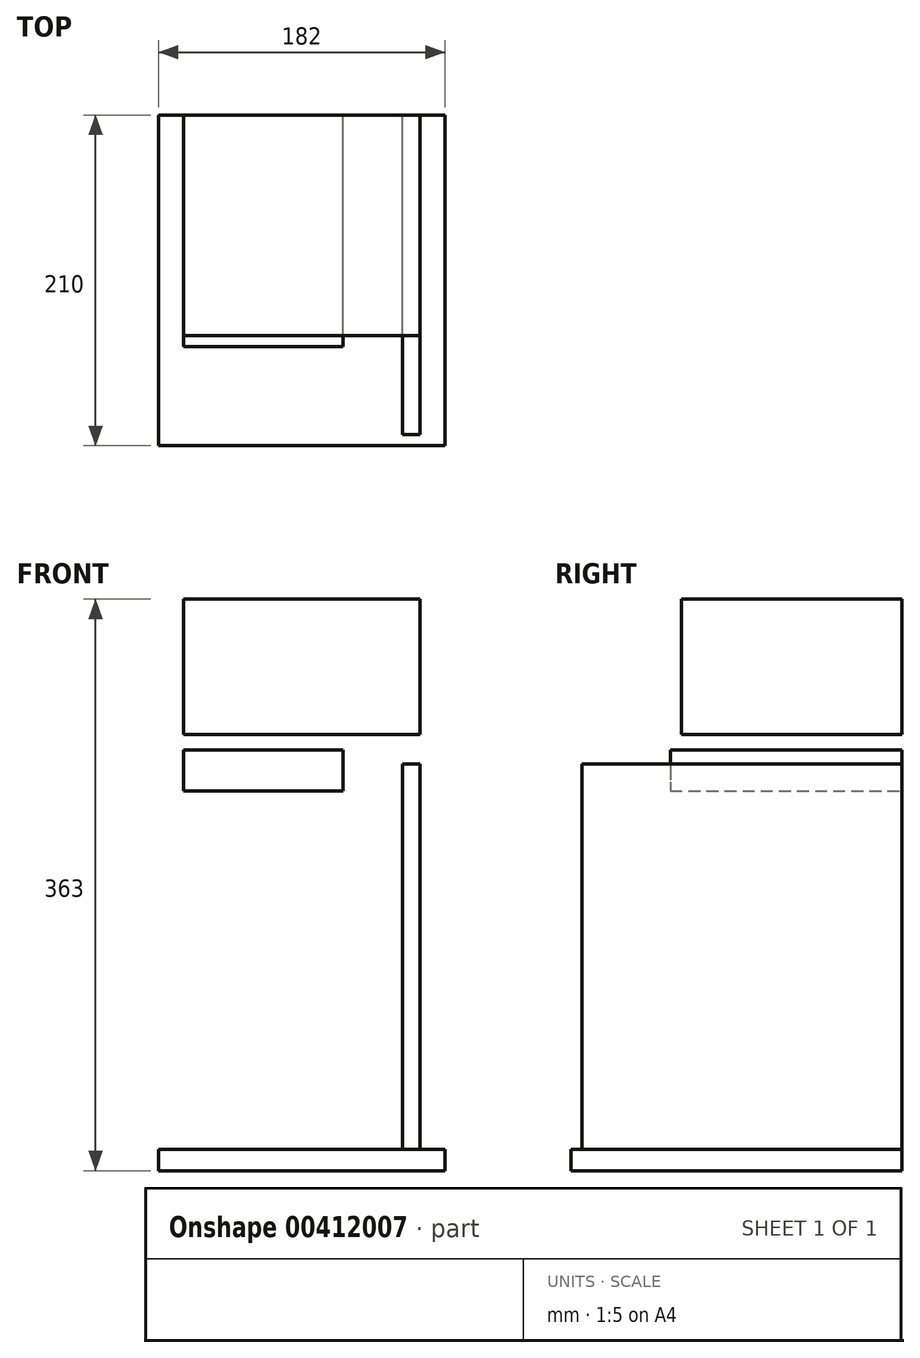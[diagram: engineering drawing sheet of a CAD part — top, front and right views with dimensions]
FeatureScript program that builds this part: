
annotation { "Feature Type Name" : "Feature", "Feature Type Description" : "" }
export const myFeature = defineFeature(function(context is Context, id is Id, definition is map)
    precondition{}
    {
        {
            var Q0;
            Q0=qCreatedBy(makeId("Front.planeOp"),FACE);
            var sketch = newSketch(context, id + "F0", { "sketchPlane" : qUnion([Q0])});
            skLineSegment(sketch, "E0.bottom", {"start": v(61.2, -118.17) * mm, "end": v(-120.8, -118.17) * mm});
            skLineSegment(sketch, "E0.top", {"start": v(61.2, -131.7) * mm, "end": v(-120.8, -131.7) * mm});
            skLineSegment(sketch, "E0.left", {"start": v(61.2, -118.17) * mm, "end": v(61.2, -131.7) * mm});
            skLineSegment(sketch, "E0.right", {"start": v(-120.8, -118.17) * mm, "end": v(-120.8, -131.7) * mm});
            skLineSegment(sketch, "E1.bottom", {"start": v(61.2, -118.17) * mm, "end": v(45.2, -118.17) * mm});
            skLineSegment(sketch, "E1.top", {"start": v(61.2, 232.3) * mm, "end": v(45.2, 232.3) * mm});
            skLineSegment(sketch, "E1.left", {"start": v(61.2, -118.17) * mm, "end": v(61.2, 232.3) * mm});
            skLineSegment(sketch, "E1.right", {"start": v(45.2, -118.17) * mm, "end": v(45.2, 232.3) * mm});
            skLineSegment(sketch, "E2.bottom", {"start": v(-120.8, -118.17) * mm, "end": v(-104.8, -118.17) * mm});
            skLineSegment(sketch, "E2.top", {"start": v(-120.8, 232.3) * mm, "end": v(-104.8, 232.3) * mm});
            skLineSegment(sketch, "E2.left", {"start": v(-120.8, -118.17) * mm, "end": v(-120.8, 232.3) * mm});
            skLineSegment(sketch, "E2.right", {"start": v(-104.8, -118.17) * mm, "end": v(-104.8, 232.3) * mm});
            skSolve(sketch);
        }
        {
            var Q0;
            Q0=makeQuery(id+"F0.imprint","IMPRINT",FACE,{"disambiguationData":[TD([[makeQuery(id+"F0.imprint","IMPRINT",EDGE,{"derivedFrom":sQuery(id+"F0.wireOp",EDGE,"E1.bottom")}),-1.0]])]});
            var Q1;
            Q1=makeQuery(id+"F0.imprint","IMPRINT",FACE,{"disambiguationData":[TD([[makeQuery(id+"F0.imprint","IMPRINT",EDGE,{"derivedFrom":sQuery(id+"F0.wireOp",EDGE,"E0.bottom")}),1.0]])]});
            var Q2;
            Q2=makeQuery(id+"F0.imprint","IMPRINT",FACE,{"disambiguationData":[TD([[makeQuery(id+"F0.imprint","IMPRINT",EDGE,{"derivedFrom":sQuery(id+"F0.wireOp",EDGE,"E2.bottom")}),1.0]])]});
            extrude(context, id + "F1", {"entities" : qUnion([Q0, Q1, Q2]), "depth" : 210 * mm});
        }
        {
            var Q0;
            Q0=qCreatedBy(makeId("Front.planeOp"),FACE);
            var sketch = newSketch(context, id + "F2", { "sketchPlane" : qUnion([Q0])});
            skLineSegment(sketch, "E3.bottom", {"start": v(45.17, 231.3) * mm, "end": v(-104.83, 231.3) * mm});
            skLineSegment(sketch, "E3.top", {"start": v(45.17, 145.3) * mm, "end": v(-104.83, 145.3) * mm});
            skLineSegment(sketch, "E3.left", {"start": v(45.17, 231.3) * mm, "end": v(45.17, 145.3) * mm});
            skLineSegment(sketch, "E3.right", {"start": v(-104.83, 231.3) * mm, "end": v(-104.83, 145.3) * mm});
            skLineSegment(sketch, "E4.bottom", {"start": v(45.2, -118.16) * mm, "end": v(34.16, -118.16) * mm});
            skLineSegment(sketch, "E4.top", {"start": v(45.2, 126.67) * mm, "end": v(34.16, 126.67) * mm});
            skLineSegment(sketch, "E4.left", {"start": v(45.2, -118.16) * mm, "end": v(45.2, 126.67) * mm});
            skLineSegment(sketch, "E4.right", {"start": v(34.16, -118.16) * mm, "end": v(34.16, 126.67) * mm});
            skLineSegment(sketch, "E5.bottom", {"start": v(-104.83, 135.54) * mm, "end": v(-3.83, 135.54) * mm});
            skLineSegment(sketch, "E5.top", {"start": v(-104.83, 109.44) * mm, "end": v(-3.83, 109.44) * mm});
            skLineSegment(sketch, "E5.left", {"start": v(-104.83, 135.54) * mm, "end": v(-104.83, 109.44) * mm});
            skLineSegment(sketch, "E5.right", {"start": v(-3.83, 135.54) * mm, "end": v(-3.83, 109.44) * mm});
            skSolve(sketch);
        }
        {
            var Q0;
            Q0=makeQuery(id+"F2.imprint","IMPRINT",FACE,{"disambiguationData":[TD([[makeQuery(id+"F2.imprint","IMPRINT",EDGE,{"derivedFrom":sQuery(id+"F2.wireOp",EDGE,"E4.bottom")}),-1.0]])]});
            extrude(context, id + "F3", {"entities" : qUnion([Q0]), "operationType" : NewBodyOperationType.ADD, "depth" : 203 * mm});
        }
        {
            var Q0;
            Q0=makeQuery(id+"F2.imprint","IMPRINT",FACE,{"disambiguationData":[TD([[makeQuery(id+"F2.imprint","IMPRINT",EDGE,{"derivedFrom":sQuery(id+"F2.wireOp",EDGE,"E5.bottom")}),-1.0]])]});
            extrude(context, id + "F4", {"entities" : qUnion([Q0]), "operationType" : NewBodyOperationType.ADD, "depth" : 147 * mm});
        }
        {
            var Q0;
            Q0=makeQuery(id+"F2.imprint","IMPRINT",FACE,{"disambiguationData":[TD([[makeQuery(id+"F2.imprint","IMPRINT",EDGE,{"derivedFrom":sQuery(id+"F2.wireOp",EDGE,"E3.bottom")}),1.0]])]});
            extrude(context, id + "F5", {"entities" : qUnion([Q0]), "operationType" : NewBodyOperationType.ADD, "depth" : 140 * mm});
        }
    });
